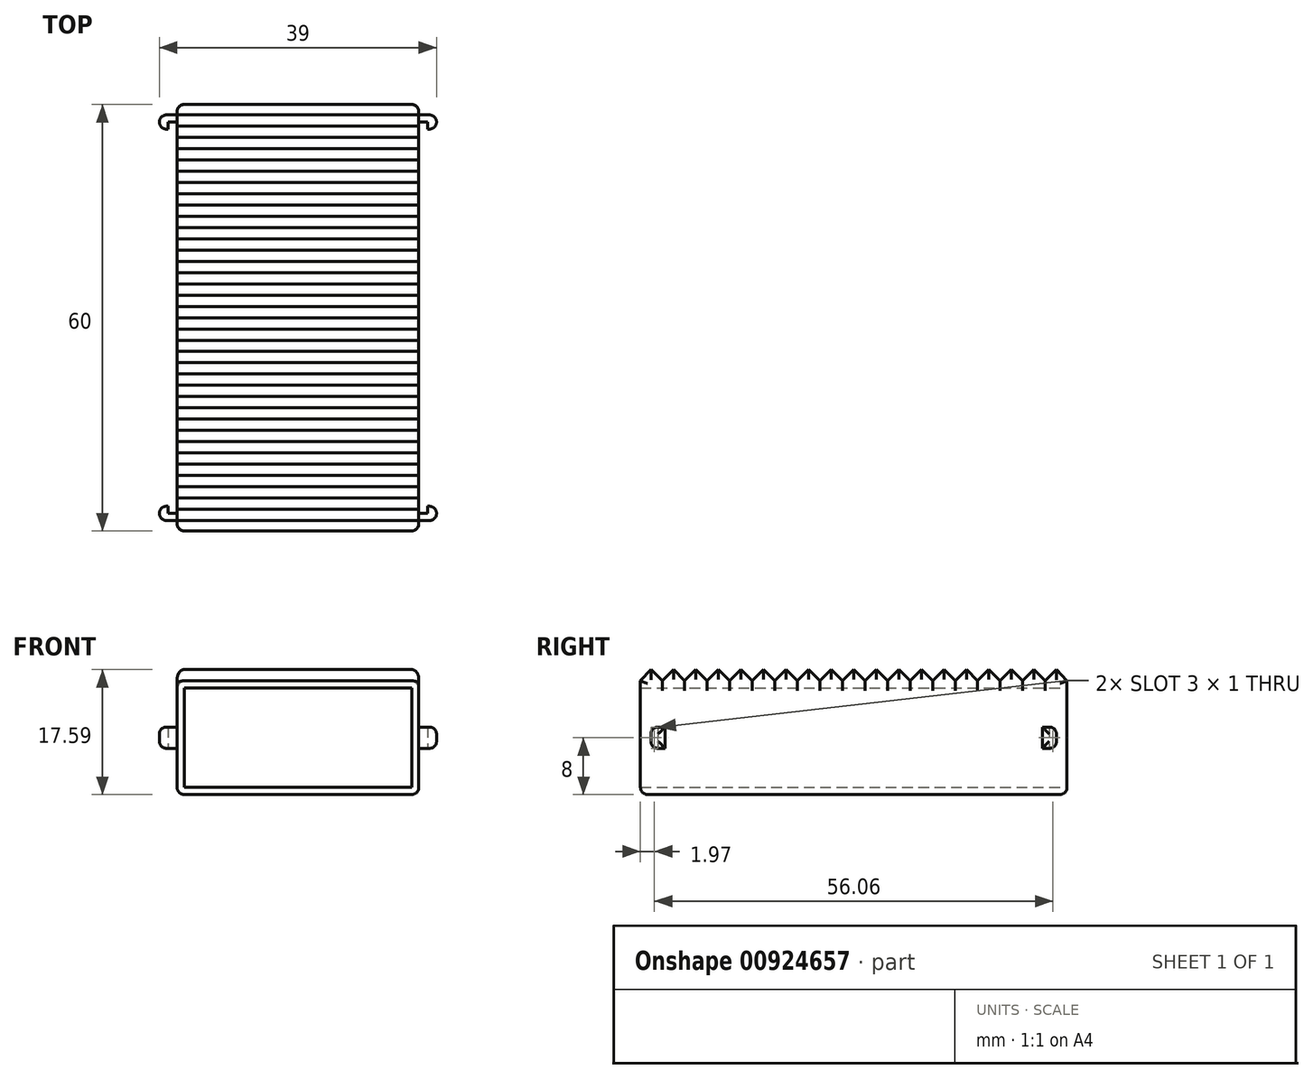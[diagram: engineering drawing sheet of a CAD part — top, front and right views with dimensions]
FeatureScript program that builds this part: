
annotation { "Feature Type Name" : "Feature", "Feature Type Description" : "" }
export const myFeature = defineFeature(function(context is Context, id is Id, definition is map)
    precondition{}
    {
        {
            var Q0;
            Q0=qCreatedBy(makeId("Front.planeOp"),FACE);
            var sketch = newSketch(context, id + "F0", { "sketchPlane" : qUnion([Q0])});
            skLineSegment(sketch, "E0.bottom", {"start": v(-17, 0) * mm, "end": v(17, 0) * mm});
            skLineSegment(sketch, "E0.top", {"start": v(-17, 16) * mm, "end": v(17, 16) * mm});
            skLineSegment(sketch, "E0.left", {"start": v(-17, 0) * mm, "end": v(-17, 16) * mm});
            skLineSegment(sketch, "E0.right", {"start": v(17, 0) * mm, "end": v(17, 16) * mm});
            skLineSegment(sketch, "E1.0", {"start": v(-16, 15) * mm, "end": v(16, 15) * mm});
            skLineSegment(sketch, "E1.1", {"start": v(-16, 1) * mm, "end": v(-16, 15) * mm});
            skLineSegment(sketch, "E1.2", {"start": v(-16, 1) * mm, "end": v(16, 1) * mm});
            skLineSegment(sketch, "E1.3", {"start": v(16, 1) * mm, "end": v(16, 15) * mm});
            skSolve(sketch);
        }
        {
            var Q0;
            Q0=makeQuery(id+"F0.imprint","IMPRINT",FACE,{"disambiguationData":[TD([[makeQuery(id+"F0.imprint","IMPRINT",EDGE,{"derivedFrom":sQuery(id+"F0.wireOp",EDGE,"E0.bottom")}),1.0]])]});
            extrude(context, id + "F1", {"entities" : qUnion([Q0]), "endBound" : BoundingType.SYMMETRIC, "depth" : 60 * mm, "offsetDistance" : 25 * mm});
        }
        {
            var Q0;
            Q0=makeQuery(id+"F1.opExtrude","SWEPT_FACE",FACE,{"disambiguationData":[OSD([sQuery(id+"F0.wireOp",EDGE,"E0.right")])]});
            var sketch = newSketch(context, id + "F2", { "sketchPlane" : qUnion([Q0])});
            skLineSegment(sketch, "E2", {"start": v(-30, 16) * mm, "end": v(30, 16) * mm});
            skLineSegment(sketch, "E3", {"start": v(28.53, 17.6) * mm, "end": v(26.94, 16.01) * mm});
            skLineSegment(sketch, "E4", {"start": v(26.94, 16.01) * mm, "end": v(25.36, 17.6) * mm});
            skLineSegment(sketch, "E5", {"start": v(25.36, 17.6) * mm, "end": v(23.77, 16.01) * mm});
            skLineSegment(sketch, "E6", {"start": v(23.77, 16.01) * mm, "end": v(22.19, 17.6) * mm});
            skLineSegment(sketch, "E7", {"start": v(22.19, 17.6) * mm, "end": v(20.6, 16.01) * mm});
            skLineSegment(sketch, "E8", {"start": v(20.6, 16.01) * mm, "end": v(19.02, 17.6) * mm});
            skLineSegment(sketch, "E9", {"start": v(19.02, 17.6) * mm, "end": v(17.43, 16) * mm});
            skLineSegment(sketch, "E10", {"start": v(17.43, 16.01) * mm, "end": v(15.85, 17.6) * mm});
            skLineSegment(sketch, "E11", {"start": v(15.85, 17.6) * mm, "end": v(14.26, 16.01) * mm});
            skLineSegment(sketch, "E12", {"start": v(14.26, 16.01) * mm, "end": v(12.68, 17.6) * mm});
            skLineSegment(sketch, "E13", {"start": v(12.68, 17.6) * mm, "end": v(11.1, 16.01) * mm});
            skLineSegment(sketch, "E14", {"start": v(11.1, 16.01) * mm, "end": v(9.5, 17.6) * mm});
            skLineSegment(sketch, "E15", {"start": v(9.5, 17.6) * mm, "end": v(7.92, 16.01) * mm});
            skLineSegment(sketch, "E16", {"start": v(7.92, 16.01) * mm, "end": v(6.34, 17.6) * mm});
            skLineSegment(sketch, "E17", {"start": v(6.34, 17.6) * mm, "end": v(4.75, 16.01) * mm});
            skLineSegment(sketch, "E18", {"start": v(4.75, 16.01) * mm, "end": v(3.17, 17.6) * mm});
            skLineSegment(sketch, "E19", {"start": v(3.17, 17.6) * mm, "end": v(1.58, 16.01) * mm});
            skLineSegment(sketch, "E20", {"start": v(1.58, 16.01) * mm, "end": v(0, 17.6) * mm});
            skLineSegment(sketch, "E21", {"start": v(28.53, 17.6) * mm, "end": v(30, 16) * mm});
            skLineSegment(sketch, "E22.MirrorCS", {"start": v(-1.58, 16.01) * mm, "end": v(0, 17.6) * mm});
            skLineSegment(sketch, "E23.MirrorCS", {"start": v(-3.17, 17.6) * mm, "end": v(-1.58, 16.01) * mm});
            skLineSegment(sketch, "E24.MirrorCS", {"start": v(-4.75, 16.01) * mm, "end": v(-3.17, 17.6) * mm});
            skLineSegment(sketch, "E25.MirrorCS", {"start": v(-9.5, 17.6) * mm, "end": v(-7.92, 16.01) * mm});
            skLineSegment(sketch, "E26.MirrorCS", {"start": v(-11.1, 16.01) * mm, "end": v(-9.5, 17.6) * mm});
            skLineSegment(sketch, "E27.MirrorCS", {"start": v(-7.92, 16.01) * mm, "end": v(-6.34, 17.6) * mm});
            skLineSegment(sketch, "E28.MirrorCS", {"start": v(-6.34, 17.6) * mm, "end": v(-4.75, 16.01) * mm});
            skLineSegment(sketch, "E29.MirrorCS", {"start": v(-28.53, 17.6) * mm, "end": v(-30, 16) * mm});
            skLineSegment(sketch, "E30.MirrorCS", {"start": v(-28.53, 17.6) * mm, "end": v(-26.94, 16.01) * mm});
            skLineSegment(sketch, "E31.MirrorCS", {"start": v(-25.36, 17.6) * mm, "end": v(-23.77, 16.01) * mm});
            skLineSegment(sketch, "E32.MirrorCS", {"start": v(-23.77, 16.01) * mm, "end": v(-22.19, 17.6) * mm});
            skLineSegment(sketch, "E33.MirrorCS", {"start": v(-26.94, 16.01) * mm, "end": v(-25.36, 17.6) * mm});
            skLineSegment(sketch, "E34.MirrorCS", {"start": v(-22.19, 17.6) * mm, "end": v(-20.6, 16.01) * mm});
            skLineSegment(sketch, "E35.MirrorCS", {"start": v(-20.6, 16.01) * mm, "end": v(-19.02, 17.6) * mm});
            skLineSegment(sketch, "E36.MirrorCS", {"start": v(-19.02, 17.6) * mm, "end": v(-17.43, 16) * mm});
            skLineSegment(sketch, "E37.MirrorCS", {"start": v(-17.43, 16.01) * mm, "end": v(-15.85, 17.6) * mm});
            skLineSegment(sketch, "E38.MirrorCS", {"start": v(-15.85, 17.6) * mm, "end": v(-14.26, 16.01) * mm});
            skLineSegment(sketch, "E39.MirrorCS", {"start": v(-14.26, 16.01) * mm, "end": v(-12.68, 17.6) * mm});
            skLineSegment(sketch, "E40.MirrorCS", {"start": v(-12.68, 17.6) * mm, "end": v(-11.1, 16.01) * mm});
            skSolve(sketch);
        }
        {
            var Q0;
            Q0=makeQuery(id+"F2.imprint","IMPRINT",FACE,{"disambiguationData":[TD([[makeQuery(id+"F2.imprint","IMPRINT",EDGE,{"derivedFrom":sQuery(id+"F2.wireOp",EDGE,"E2")}),1.0]])]});
            extrude(context, id + "F3", {"entities" : qUnion([Q0]), "operationType" : NewBodyOperationType.ADD, "oppositeDirection" : true, "depth" : 34 * mm, "offsetDistance" : 25 * mm});
        }
        {
            var Q0;
            Q0=makeQuery(id+"F3.boolean.opBoolean","MERGE",FACE,{"derivedFrom":[makeQuery(id+"F1.opExtrude","SWEPT_FACE",FACE,{"disambiguationData":[OSD([sQuery(id+"F0.wireOp",EDGE,"E0.right")])]}),makeQuery(id+"F3.opExtrude","CAP_FACE",FACE,{"disambiguationData":[OSD([sQuery(id+"F2.wireOp",EDGE,"E2"),sQuery(id+"F2.wireOp",EDGE,"E3"),sQuery(id+"F2.wireOp",EDGE,"E4"),sQuery(id+"F2.wireOp",EDGE,"E5"),sQuery(id+"F2.wireOp",EDGE,"E6"),sQuery(id+"F2.wireOp",EDGE,"E7"),sQuery(id+"F2.wireOp",EDGE,"E8"),sQuery(id+"F2.wireOp",EDGE,"E9"),sQuery(id+"F2.wireOp",EDGE,"E10"),sQuery(id+"F2.wireOp",EDGE,"E11"),sQuery(id+"F2.wireOp",EDGE,"E12"),sQuery(id+"F2.wireOp",EDGE,"E13"),sQuery(id+"F2.wireOp",EDGE,"E14"),sQuery(id+"F2.wireOp",EDGE,"E15"),sQuery(id+"F2.wireOp",EDGE,"E16"),sQuery(id+"F2.wireOp",EDGE,"E17"),sQuery(id+"F2.wireOp",EDGE,"E18"),sQuery(id+"F2.wireOp",EDGE,"E19"),sQuery(id+"F2.wireOp",EDGE,"E20"),sQuery(id+"F2.wireOp",EDGE,"E21"),sQuery(id+"F2.wireOp",EDGE,"E22.MirrorCS"),sQuery(id+"F2.wireOp",EDGE,"E23.MirrorCS"),sQuery(id+"F2.wireOp",EDGE,"E24.MirrorCS"),sQuery(id+"F2.wireOp",EDGE,"E25.MirrorCS"),sQuery(id+"F2.wireOp",EDGE,"E26.MirrorCS"),sQuery(id+"F2.wireOp",EDGE,"E27.MirrorCS"),sQuery(id+"F2.wireOp",EDGE,"E28.MirrorCS"),sQuery(id+"F2.wireOp",EDGE,"E29.MirrorCS"),sQuery(id+"F2.wireOp",EDGE,"E30.MirrorCS"),sQuery(id+"F2.wireOp",EDGE,"E31.MirrorCS"),sQuery(id+"F2.wireOp",EDGE,"E32.MirrorCS"),sQuery(id+"F2.wireOp",EDGE,"E33.MirrorCS"),sQuery(id+"F2.wireOp",EDGE,"E34.MirrorCS"),sQuery(id+"F2.wireOp",EDGE,"E35.MirrorCS"),sQuery(id+"F2.wireOp",EDGE,"E36.MirrorCS"),sQuery(id+"F2.wireOp",EDGE,"E37.MirrorCS"),sQuery(id+"F2.wireOp",EDGE,"E38.MirrorCS"),sQuery(id+"F2.wireOp",EDGE,"E39.MirrorCS"),sQuery(id+"F2.wireOp",EDGE,"E40.MirrorCS")])],"isStart":true})]});
            var Q1;
            Q1=makeQuery(id+"F1.opExtrude","SWEPT_FACE",FACE,{"disambiguationData":[OSD([sQuery(id+"F0.wireOp",EDGE,"E0.bottom")])]});
            var Q2;
            Q2=makeQuery(id+"F3.boolean.opBoolean","MERGE",FACE,{"derivedFrom":[makeQuery(id+"F1.opExtrude","SWEPT_FACE",FACE,{"disambiguationData":[OSD([sQuery(id+"F0.wireOp",EDGE,"E0.left")])]}),makeQuery(id+"F3.opExtrude","CAP_FACE",FACE,{"disambiguationData":[OSD([sQuery(id+"F2.wireOp",EDGE,"E2"),sQuery(id+"F2.wireOp",EDGE,"E3"),sQuery(id+"F2.wireOp",EDGE,"E4"),sQuery(id+"F2.wireOp",EDGE,"E5"),sQuery(id+"F2.wireOp",EDGE,"E6"),sQuery(id+"F2.wireOp",EDGE,"E7"),sQuery(id+"F2.wireOp",EDGE,"E8"),sQuery(id+"F2.wireOp",EDGE,"E9"),sQuery(id+"F2.wireOp",EDGE,"E10"),sQuery(id+"F2.wireOp",EDGE,"E11"),sQuery(id+"F2.wireOp",EDGE,"E12"),sQuery(id+"F2.wireOp",EDGE,"E13"),sQuery(id+"F2.wireOp",EDGE,"E14"),sQuery(id+"F2.wireOp",EDGE,"E15"),sQuery(id+"F2.wireOp",EDGE,"E16"),sQuery(id+"F2.wireOp",EDGE,"E17"),sQuery(id+"F2.wireOp",EDGE,"E18"),sQuery(id+"F2.wireOp",EDGE,"E19"),sQuery(id+"F2.wireOp",EDGE,"E20"),sQuery(id+"F2.wireOp",EDGE,"E21"),sQuery(id+"F2.wireOp",EDGE,"E22.MirrorCS"),sQuery(id+"F2.wireOp",EDGE,"E23.MirrorCS"),sQuery(id+"F2.wireOp",EDGE,"E24.MirrorCS"),sQuery(id+"F2.wireOp",EDGE,"E25.MirrorCS"),sQuery(id+"F2.wireOp",EDGE,"E26.MirrorCS"),sQuery(id+"F2.wireOp",EDGE,"E27.MirrorCS"),sQuery(id+"F2.wireOp",EDGE,"E28.MirrorCS"),sQuery(id+"F2.wireOp",EDGE,"E29.MirrorCS"),sQuery(id+"F2.wireOp",EDGE,"E30.MirrorCS"),sQuery(id+"F2.wireOp",EDGE,"E31.MirrorCS"),sQuery(id+"F2.wireOp",EDGE,"E32.MirrorCS"),sQuery(id+"F2.wireOp",EDGE,"E33.MirrorCS"),sQuery(id+"F2.wireOp",EDGE,"E34.MirrorCS"),sQuery(id+"F2.wireOp",EDGE,"E35.MirrorCS"),sQuery(id+"F2.wireOp",EDGE,"E36.MirrorCS"),sQuery(id+"F2.wireOp",EDGE,"E37.MirrorCS"),sQuery(id+"F2.wireOp",EDGE,"E38.MirrorCS"),sQuery(id+"F2.wireOp",EDGE,"E39.MirrorCS"),sQuery(id+"F2.wireOp",EDGE,"E40.MirrorCS")])],"isStart":false})]});
            fillet(context, id + "F4", {"entities" : qUnion([Q0, Q1, Q2]), "radius" : 1 * mm, "tangentPropagation" : true, "allowEdgeOverflow" : false});
        }
        {
            var Q0;
            Q0=qCreatedBy(makeId("Top.planeOp"),FACE);
            cPlane(context, id + "F5", {"entities" : qUnion([Q0]), "cplaneType" : CPlaneType.OFFSET, "offset" : 8 * mm, "width" : 150 * mm, "height" : 150 * mm});
        }
        {
            var Q0;
            Q0=qCreatedBy(id+"F5.planeOp",FACE);
            var sketch = newSketch(context, id + "F6", { "sketchPlane" : qUnion([Q0])});
            skLineSegment(sketch, "E41", {"start": v(17, -28.53) * mm, "end": v(19.5, -28.53) * mm});
            skLineSegment(sketch, "E42", {"start": v(19.5, -28.53) * mm, "end": v(19.5, -26.53) * mm});
            skLineSegment(sketch, "E43", {"start": v(19.5, -26.53) * mm, "end": v(18.25, -26.53) * mm});
            skPoint(sketch, "E43.endSnap0", {"position": v(18.25, -28.53) * mm});
            skLineSegment(sketch, "E44", {"start": v(18.25, -26.53) * mm, "end": v(18.25, -27.53) * mm});
            skLineSegment(sketch, "E45", {"start": v(18.25, -27.53) * mm, "end": v(17, -27.53) * mm});
            skLineSegment(sketch, "E46", {"start": v(17, -27.53) * mm, "end": v(17, -28.53) * mm});
            skLineSegment(sketch, "E47.MirrorCS", {"start": v(-17, -28.53) * mm, "end": v(-19.5, -28.53) * mm});
            skLineSegment(sketch, "E48.MirrorCS", {"start": v(-19.5, -28.53) * mm, "end": v(-19.5, -26.53) * mm});
            skLineSegment(sketch, "E49.MirrorCS", {"start": v(-17, -27.53) * mm, "end": v(-17, -28.53) * mm});
            skLineSegment(sketch, "E50.MirrorCS", {"start": v(-18.25, -27.53) * mm, "end": v(-17, -27.53) * mm});
            skLineSegment(sketch, "E51.MirrorCS", {"start": v(-18.25, -26.53) * mm, "end": v(-18.25, -27.53) * mm});
            skLineSegment(sketch, "E52.MirrorCS", {"start": v(-19.5, -26.53) * mm, "end": v(-18.25, -26.53) * mm});
            skLineSegment(sketch, "E53.MirrorCS", {"start": v(-19.5, 28.53) * mm, "end": v(-19.5, 26.53) * mm});
            skLineSegment(sketch, "E54.MirrorCS", {"start": v(-19.5, 26.53) * mm, "end": v(-18.25, 26.53) * mm});
            skLineSegment(sketch, "E55.MirrorCS", {"start": v(-18.25, 26.53) * mm, "end": v(-18.25, 27.53) * mm});
            skLineSegment(sketch, "E56.MirrorCS", {"start": v(-18.25, 27.53) * mm, "end": v(-17, 27.53) * mm});
            skLineSegment(sketch, "E57.MirrorCS", {"start": v(-17, 28.53) * mm, "end": v(-19.5, 28.53) * mm});
            skLineSegment(sketch, "E58.MirrorCS", {"start": v(18.25, 26.53) * mm, "end": v(18.25, 27.53) * mm});
            skLineSegment(sketch, "E59.MirrorCS", {"start": v(19.5, 26.53) * mm, "end": v(18.25, 26.53) * mm});
            skLineSegment(sketch, "E60.MirrorCS", {"start": v(19.5, 28.53) * mm, "end": v(19.5, 26.53) * mm});
            skLineSegment(sketch, "E61.MirrorCS", {"start": v(17, 28.53) * mm, "end": v(19.5, 28.53) * mm});
            skLineSegment(sketch, "E62.MirrorCS", {"start": v(17, 27.53) * mm, "end": v(17, 28.53) * mm});
            skLineSegment(sketch, "E63.MirrorCS", {"start": v(18.25, 27.53) * mm, "end": v(17, 27.53) * mm});
            skLineSegment(sketch, "E64", {"start": v(-17, 27.53) * mm, "end": v(-17, 28.53) * mm});
            skSolve(sketch);
        }
        {
            var Q0;
            Q0 = qSketchRegion(id + "F6", true);
            extrude(context, id + "F7", {"entities" : qUnion([Q0]), "operationType" : NewBodyOperationType.ADD, "endBound" : BoundingType.SYMMETRIC, "depth" : 3 * mm, "offsetDistance" : 25 * mm});
        }
        {
            var Q0;
            Q0=makeQuery(id+"F7.opExtrude","SWEPT_EDGE",EDGE,{"disambiguationData":[OSD([sQuery(id+"F6.wireOp",EDGE,"E53.MirrorCS"),sQuery(id+"F6.wireOp",EDGE,"E57.MirrorCS")])]});
            var Q1;
            Q1=makeQuery(id+"F7.opExtrude","CAP_EDGE",EDGE,{"disambiguationData":[OSD([sQuery(id+"F6.wireOp",EDGE,"E57.MirrorCS")])],"isStart":false});
            var Q2;
            Q2=makeQuery(id+"F7.opExtrude","CAP_EDGE",EDGE,{"disambiguationData":[OSD([sQuery(id+"F6.wireOp",EDGE,"E57.MirrorCS")])],"isStart":true});
            var Q3;
            Q3=makeQuery(id+"F7.opExtrude","SWEPT_FACE",FACE,{"disambiguationData":[OSD([sQuery(id+"F6.wireOp",EDGE,"E53.MirrorCS")])]});
            var Q4;
            Q4=makeQuery(id+"F7.opExtrude","CAP_EDGE",EDGE,{"disambiguationData":[OSD([sQuery(id+"F6.wireOp",EDGE,"E61.MirrorCS")])],"isStart":false});
            var Q5;
            Q5=makeQuery(id+"F7.opExtrude","CAP_EDGE",EDGE,{"disambiguationData":[OSD([sQuery(id+"F6.wireOp",EDGE,"E61.MirrorCS")])],"isStart":true});
            var Q6;
            Q6=makeQuery(id+"F7.opExtrude","SWEPT_FACE",FACE,{"disambiguationData":[OSD([sQuery(id+"F6.wireOp",EDGE,"E60.MirrorCS")])]});
            var Q7;
            Q7=makeQuery(id+"F7.opExtrude","CAP_EDGE",EDGE,{"disambiguationData":[OSD([sQuery(id+"F6.wireOp",EDGE,"E41")])],"isStart":false});
            var Q8;
            Q8=makeQuery(id+"F7.opExtrude","CAP_EDGE",EDGE,{"disambiguationData":[OSD([sQuery(id+"F6.wireOp",EDGE,"E41")])],"isStart":true});
            var Q9;
            Q9=makeQuery(id+"F7.opExtrude","SWEPT_FACE",FACE,{"disambiguationData":[OSD([sQuery(id+"F6.wireOp",EDGE,"E42")])]});
            var Q10;
            Q10=makeQuery(id+"F7.opExtrude","SWEPT_FACE",FACE,{"disambiguationData":[OSD([sQuery(id+"F6.wireOp",EDGE,"E48.MirrorCS")])]});
            var Q11;
            Q11=makeQuery(id+"F7.opExtrude","CAP_EDGE",EDGE,{"disambiguationData":[OSD([sQuery(id+"F6.wireOp",EDGE,"E47.MirrorCS")])],"isStart":false});
            var Q12;
            Q12=makeQuery(id+"F7.opExtrude","CAP_EDGE",EDGE,{"disambiguationData":[OSD([sQuery(id+"F6.wireOp",EDGE,"E47.MirrorCS")])],"isStart":true});
            fillet(context, id + "F8", {"entities" : qUnion([Q0, Q1, Q2, Q3, Q4, Q5, Q6, Q7, Q8, Q9, Q10, Q11, Q12]), "radius" : 1 * mm, "tangentPropagation" : true, "allowEdgeOverflow" : false});
        }
    });
